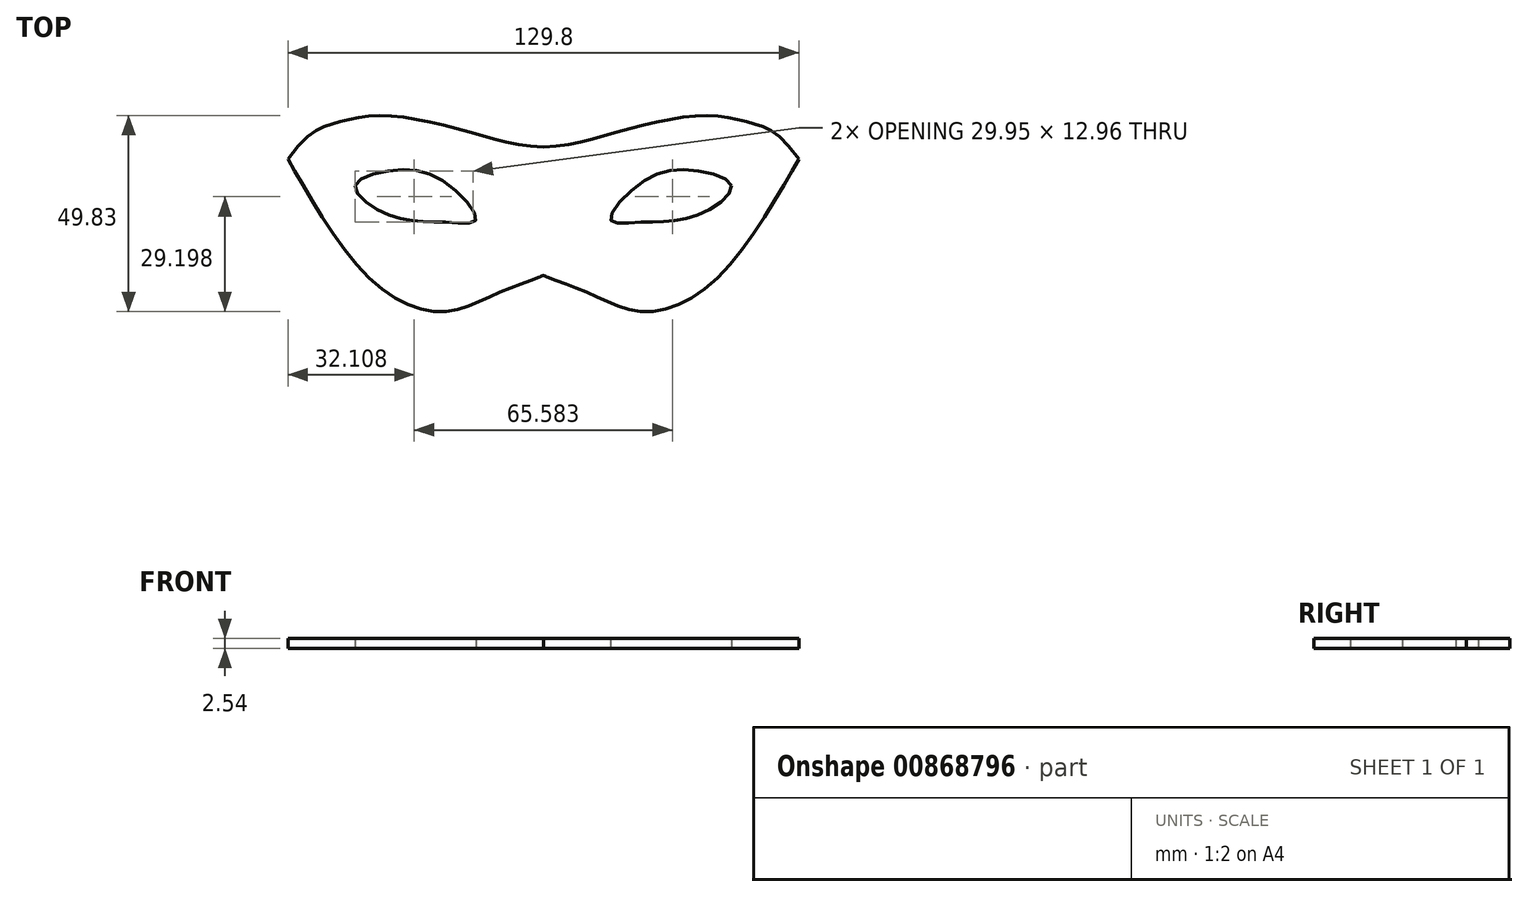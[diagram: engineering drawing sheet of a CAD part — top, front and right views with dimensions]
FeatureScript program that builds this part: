
annotation { "Feature Type Name" : "Feature", "Feature Type Description" : "" }
export const myFeature = defineFeature(function(context is Context, id is Id, definition is map)
    precondition{}
    {
        {
            var Q0;
            Q0=qCreatedBy(makeId("Top.planeOp"),FACE);
            var sketch = newSketch(context, id + "F0", { "sketchPlane" : qUnion([Q0])});
            skFitSpline(sketch, "E0", {"points": [v(-64.9, 13.96) * mm, v(-52.81, 23.17) * mm, v(-40.72, 25.04) * mm, v(-19.43, 21.01) * mm, v(0, 16.98) * mm], "startDerivative": vector(64.25, 90.32) * mm, "endDerivative": vector(75.52, -3.61) * mm});
            skFitSpline(sketch, "E1", {"points": [v(-64.9, 13.96) * mm, v(-44.75, -15.69) * mm, v(-24.9, -24.75) * mm, v(-11.08, -19.86) * mm, v(0, -15.54) * mm], "startDerivative": vector(37.63, -63.67) * mm, "endDerivative": vector(46.75, 21.18) * mm});
            skFitSpline(sketch, "E2", {"points": [v(-47.76, 7.28) * mm, v(-37.8, 11.15) * mm, v(-24.9, 8.06) * mm, v(-17.12, -1.44) * mm, v(-23.17, -2.16) * mm, v(-32.38, -1.73) * mm, v(-42.16, 1.15) * mm, v(-47.76, 7.28) * mm]});
            skFitSpline(sketch, "E3.MirrorCS", {"points": [v(64.9, 13.96) * mm, v(52.81, 23.17) * mm, v(40.72, 25.04) * mm, v(19.43, 21.01) * mm, v(0, 16.98) * mm], "startDerivative": vector(-64.25, 90.32) * mm, "endDerivative": vector(-75.52, -3.61) * mm});
            skFitSpline(sketch, "E4.MirrorC", {"points": [v(47.76, 7.28) * mm, v(37.8, 11.15) * mm, v(24.9, 8.06) * mm, v(17.12, -1.44) * mm, v(23.17, -2.16) * mm, v(32.38, -1.73) * mm, v(42.16, 1.15) * mm, v(47.76, 7.28) * mm]});
            skFitSpline(sketch, "E5.MirrorCS", {"points": [v(64.9, 13.96) * mm, v(44.75, -15.69) * mm, v(24.9, -24.75) * mm, v(11.08, -19.86) * mm, v(0, -15.54) * mm], "startDerivative": vector(-37.63, -63.67) * mm, "endDerivative": vector(-46.75, 21.18) * mm});
            skArc(sketch, "E6.filletArc", {"start": v(0.97, -15.96) * mm, "mid": v(0, -15.77) * mm, "end": v(-0.97, -15.96) * mm});
            skSolve(sketch);
        }
        {
            var Q0;
            Q0=makeQuery(id+"F0.imprint","IMPRINT",FACE,{"disambiguationData":[TD([[makeQuery(id+"F0.imprint","IMPRINT",EDGE,{"derivedFrom":sQuery(id+"F0.wireOp",EDGE,"E0")}),-1.0]])]});
            extrude(context, id + "F1", {"entities" : qUnion([Q0]), "depth" : 2.54 * mm, "offsetDistance" : 25.4 * mm});
        }
    });
